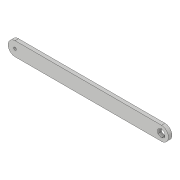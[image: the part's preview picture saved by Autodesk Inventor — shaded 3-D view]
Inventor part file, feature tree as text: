
AUTODESK INVENTOR PART (.ipt)
format: ipt  version: 2018 (Build 220112000, 112)  size: 87,552 bytes
history: native  units: in
note: dims shown in document units (in); Inventor stores cm internally (conversion verified against a paired STEP export)
features: extrude x1, sketch x1
ambient origin geometry x8: Origin, YZ Plane, XZ Plane, XY Plane, X Axis, Y Axis, Z Axis, Center Point
bodies: Solid1 (feature_tree)
feature tree (2):
  extrude  "Extrusion1"  Depth=0.25in
  sketch  "Sketch1"  dims[d0=0.5in d1=0.2in d2=10.5in d3=1.0in d4=0.25in d5=0.0in]
